annotation { "Feature Type Name" : "Feature", "Feature Type Description" : "" }
export const myFeature = defineFeature(function(context is Context, id is Id, definition is map)
    precondition{}
    {
        {
            var Q0;
            Q0=qCreatedBy(makeId("Top.planeOp"),FACE);
            var sketch = newSketch(context, id + "F0", { "sketchPlane" : qUnion([Q0])});
            skLineSegment(sketch, "E0.bottom", {"start": v(-44.45, 25.4) * mm, "end": v(44.45, 25.4) * mm});
            skLineSegment(sketch, "E0.top", {"start": v(-44.45, -25.4) * mm, "end": v(44.45, -25.4) * mm});
            skLineSegment(sketch, "E0.left", {"start": v(-44.45, 25.4) * mm, "end": v(-44.45, -25.4) * mm});
            skLineSegment(sketch, "E0.right", {"start": v(44.45, 25.4) * mm, "end": v(44.45, -25.4) * mm});
            skPoint(sketch, "E0.middle", {"position": v(0, 0) * mm});
            skSolve(sketch);
        }
        {
            var Q0;
            Q0=makeQuery(id+"F0.imprint","IMPRINT",FACE,{"disambiguationData":[TD([[makeQuery(id+"F0.imprint","IMPRINT",EDGE,{"derivedFrom":sQuery(id+"F0.wireOp",EDGE,"E0.bottom")}),-1.0]])]});
            extrude(context, id + "F1", {"entities" : qUnion([Q0]), "depth" : 1 * mm, "offsetDistance" : 25 * mm});
        }
        {
            var Q0;
            Q0=makeQuery(id+"F1.opExtrude","CAP_FACE",FACE,{"disambiguationData":[OSD([sQuery(id+"F0.wireOp",EDGE,"E0.bottom"),sQuery(id+"F0.wireOp",EDGE,"E0.top"),sQuery(id+"F0.wireOp",EDGE,"E0.left"),sQuery(id+"F0.wireOp",EDGE,"E0.right")])],"isStart":false});
            var sketch = newSketch(context, id + "F2", { "sketchPlane" : qUnion([Q0])});
            skText(sketch, "E1", { "text": "Andrea Szikszay", "fontName": "AllertaStencil-Regular.ttf"});
            skText(sketch, "E2", { "text": "Engineering Student", "fontName": "AllertaStencil-Regular.ttf"});
            skText(sketch, "E3", { "text": "C: 813 368 4735\<email>", "fontName": "AllertaStencil-Regular.ttf"});
            const initialGuessF2  = {"E1": [-0.03975, 0.0119, 1, 0, 0.00609], "E2": [-0.03975, 0.0037, 1, 0, 0.00422], "E3": [-0.03975, -0.01407, 1, 0, 0.00352]};
            skSetInitialGuess(sketch, initialGuessF2);
            skSolve(sketch);
        }
        {
            var Q0;
            Q0 = qSketchRegion(id + "F2", true);
            extrude(context, id + "F3", {"entities" : qUnion([Q0]), "operationType" : NewBodyOperationType.REMOVE, "endBound" : BoundingType.THROUGH_ALL, "oppositeDirection" : true, "depth" : 0.5 * mm, "offsetDistance" : 25 * mm});
        }
        {
            var Q0;
            {var subQ0=sQuery(id+"F0.wireOp",EDGE,"E0.bottom");var subQ1=sQuery(id+"F0.wireOp",EDGE,"E0.top");var subQ2=sQuery(id+"F0.wireOp",EDGE,"E0.left");var subQ3=sQuery(id+"F0.wireOp",EDGE,"E0.right");Q0=makeQuery(id+"F3.boolean.opBoolean","SPLIT",FACE,{"disambiguationData":[TD([makeQuery(id+"F1.opExtrude","SWEPT_FACE",FACE,{"disambiguationData":[OSD([subQ0])]})])],"derivedFrom":makeQuery(id+"F1.opExtrude","CAP_FACE",FACE,{"disambiguationData":[OSD([subQ0,subQ1,subQ2,subQ3])],"isStart":false})});}
            var sketch = newSketch(context, id + "F4", { "sketchPlane" : qUnion([Q0])});
            skCircle(sketch, "E4", {"center": v(40.29, 20.44) * mm, "radius": 1.75 * mm});
            skFitSpline(sketch, "E5", {"points": [v(42.4, 20.71) * mm, v(43.2, 21.1) * mm, v(43.65, 20.91) * mm, v(43.3, 20.56) * mm, v(42.4, 20.71) * mm]});
            skFitSpline(sketch, "E6", {"points": [v(42.47, 19.63) * mm, v(43.35, 19.68) * mm, v(43.65, 19.2) * mm, v(43.23, 19.15) * mm, v(42.47, 19.63) * mm]});
            skFitSpline(sketch, "E7", {"points": [v(41.94, 18.85) * mm, v(42.72, 18.54) * mm, v(42.72, 18.14) * mm, v(42.22, 18.19) * mm, v(41.94, 18.85) * mm]});
            skFitSpline(sketch, "E8", {"points": [v(41.06, 18.44) * mm, v(41.56, 17.91) * mm, v(41.38, 17.18) * mm, v(40.9, 17.48) * mm, v(41.06, 18.44) * mm]});
            skFitSpline(sketch, "E9", {"points": [v(39.97, 18.27) * mm, v(40.2, 17.6) * mm, v(39.87, 17.18) * mm, v(39.54, 17.58) * mm, v(39.97, 18.27) * mm]});
            skFitSpline(sketch, "E10", {"points": [v(38.96, 18.74) * mm, v(38.7, 17.94) * mm, v(38.15, 17.94) * mm, v(38.2, 18.42) * mm, v(38.96, 18.74) * mm]});
            skFitSpline(sketch, "E11", {"points": [v(38.36, 19.65) * mm, v(38, 19.2) * mm, v(37.47, 19.12) * mm, v(37.47, 19.43) * mm, v(38.36, 19.65) * mm]});
            skFitSpline(sketch, "E12", {"points": [v(38.13, 20.54) * mm, v(37.45, 20.3) * mm, v(36.94, 20.56) * mm, v(37.3, 20.84) * mm, v(38.13, 20.54) * mm]});
            skFitSpline(sketch, "E13", {"points": [v(38.5, 21.7) * mm, v(37.75, 21.72) * mm, v(37.52, 22.15) * mm, v(37.95, 22.23) * mm, v(38.5, 21.7) * mm]});
            skFitSpline(sketch, "E14", {"points": [v(39.16, 22.3) * mm, v(38.53, 22.5) * mm, v(38.5, 22.98) * mm, v(38.89, 22.96) * mm, v(39.16, 22.3) * mm]});
            skFitSpline(sketch, "E15", {"points": [v(39.95, 22.55) * mm, v(39.57, 23.08) * mm, v(39.7, 23.69) * mm, v(40.15, 23.41) * mm, v(39.95, 22.55) * mm]});
            skFitSpline(sketch, "E16", {"points": [v(40.9, 22.5) * mm, v(40.84, 23.38) * mm, v(41.3, 23.7) * mm, v(41.54, 23.27) * mm, v(40.9, 22.5) * mm]});
            skFitSpline(sketch, "E17", {"points": [v(41.99, 21.84) * mm, v(42.37, 22.65) * mm, v(43.06, 22.67) * mm, v(43.04, 22.23) * mm, v(41.99, 21.84) * mm]});
            skFitSpline(sketch, "E18", {"points": [v(42.44, 17.04) * mm, v(43.25, 10.05) * mm, v(40.73, -24.15) * mm, v(39.76, -23.74) * mm, v(40.49, -23.01) * mm, v(42.85, 3.64) * mm, v(41.98, 16.43) * mm, v(42.44, 17.04) * mm]});
            skFitSpline(sketch, "E19", {"points": [v(42.64, 6.87) * mm, v(40.68, 8.3) * mm, v(40.1, 7.98) * mm, v(41.12, 7.2) * mm, v(42.64, 6.87) * mm]});
            skSolve(sketch);
        }
        {
            var Q0;
            Q0 = qSketchRegion(id + "F4", true);
            extrude(context, id + "F5", {"entities" : qUnion([Q0]), "operationType" : NewBodyOperationType.REMOVE, "oppositeDirection" : true, "depth" : 25 * mm, "offsetDistance" : 25 * mm});
        }
        {
            var Q0;
            {var subQ0=sQuery(id+"F0.wireOp",EDGE,"E0.bottom");var subQ1=sQuery(id+"F0.wireOp",EDGE,"E0.top");var subQ2=sQuery(id+"F0.wireOp",EDGE,"E0.left");var subQ3=sQuery(id+"F0.wireOp",EDGE,"E0.right");Q0=makeQuery(id+"F3.boolean.opBoolean","SPLIT",FACE,{"disambiguationData":[TD([makeQuery(id+"F1.opExtrude","SWEPT_FACE",FACE,{"disambiguationData":[OSD([subQ0])]})])],"derivedFrom":makeQuery(id+"F1.opExtrude","CAP_FACE",FACE,{"disambiguationData":[OSD([subQ0,subQ1,subQ2,subQ3])],"isStart":false})});}
            var sketch = newSketch(context, id + "F6", { "sketchPlane" : qUnion([Q0])});
            skCircle(sketch, "E20", {"center": v(38.48, 14.45) * mm, "radius": 1.5 * mm});
            skFitSpline(sketch, "E21", {"points": [v(40.28, 14.68) * mm, v(40.98, 15) * mm, v(41.37, 14.85) * mm, v(41.06, 14.55) * mm, v(40.28, 14.68) * mm]});
            skFitSpline(sketch, "E22", {"points": [v(40.35, 13.75) * mm, v(41.1, 13.8) * mm, v(41.37, 13.38) * mm, v(41, 13.34) * mm, v(40.35, 13.75) * mm]});
            skFitSpline(sketch, "E23", {"points": [v(39.9, 13.08) * mm, v(40.57, 12.82) * mm, v(40.57, 12.47) * mm, v(40.13, 12.52) * mm, v(39.9, 13.08) * mm]});
            skFitSpline(sketch, "E24", {"points": [v(39.14, 12.73) * mm, v(39.57, 12.28) * mm, v(39.42, 11.65) * mm, v(39, 11.91) * mm, v(39.14, 12.73) * mm]});
            skFitSpline(sketch, "E25", {"points": [v(38.2, 12.58) * mm, v(38.4, 12.02) * mm, v(38.12, 11.65) * mm, v(37.84, 12) * mm, v(38.2, 12.58) * mm]});
            skFitSpline(sketch, "E26", {"points": [v(37.34, 13) * mm, v(37.13, 12.3) * mm, v(36.65, 12.3) * mm, v(36.7, 12.71) * mm, v(37.34, 13) * mm]});
            skFitSpline(sketch, "E27", {"points": [v(36.82, 13.77) * mm, v(36.52, 13.38) * mm, v(36.07, 13.32) * mm, v(36.07, 13.58) * mm, v(36.82, 13.77) * mm]});
            skFitSpline(sketch, "E28", {"points": [v(36.63, 14.53) * mm, v(36.05, 14.33) * mm, v(35.61, 14.55) * mm, v(35.92, 14.79) * mm, v(36.63, 14.53) * mm]});
            skFitSpline(sketch, "E29", {"points": [v(36.95, 15.52) * mm, v(36.3, 15.55) * mm, v(36.11, 15.91) * mm, v(36.48, 15.98) * mm, v(36.95, 15.52) * mm]});
            skFitSpline(sketch, "E30", {"points": [v(37.52, 16.04) * mm, v(36.98, 16.22) * mm, v(36.95, 16.63) * mm, v(37.28, 16.6) * mm, v(37.52, 16.04) * mm]});
            skFitSpline(sketch, "E31", {"points": [v(38.19, 16.26) * mm, v(37.86, 16.71) * mm, v(37.97, 17.23) * mm, v(38.36, 17) * mm, v(38.19, 16.26) * mm]});
            skFitSpline(sketch, "E32", {"points": [v(39, 16.2) * mm, v(38.95, 16.97) * mm, v(39.35, 17.24) * mm, v(39.55, 16.87) * mm, v(39, 16.2) * mm]});
            skFitSpline(sketch, "E33", {"points": [v(39.94, 15.65) * mm, v(40.26, 16.34) * mm, v(40.85, 16.35) * mm, v(40.84, 15.98) * mm, v(39.94, 15.65) * mm]});
            skFitSpline(sketch, "E34", {"points": [v(39.2, 10.97) * mm, v(35.1, -7.56) * mm, v(34.84, -23.3) * mm, v(36.05, -23.2) * mm, v(35.04, -21.42) * mm, v(38.45, 7.4) * mm, v(39.39, 10.9) * mm, v(39.2, 10.97) * mm]});
            skFitSpline(sketch, "E35", {"points": [v(37.25, 2.33) * mm, v(38.56, 2.97) * mm, v(39.29, 2.56) * mm, v(38.68, 2.36) * mm, v(37.25, 2.33) * mm]});
            skSolve(sketch);
        }
        {
            var Q0;
            Q0 = qSketchRegion(id + "F6", true);
            extrude(context, id + "F7", {"entities" : qUnion([Q0]), "operationType" : NewBodyOperationType.REMOVE, "oppositeDirection" : true, "depth" : 25 * mm, "offsetDistance" : 25 * mm});
        }
        {
            var Q0;
            {var subQ0=sQuery(id+"F0.wireOp",EDGE,"E0.bottom");var subQ1=sQuery(id+"F0.wireOp",EDGE,"E0.top");var subQ2=sQuery(id+"F0.wireOp",EDGE,"E0.left");var subQ3=sQuery(id+"F0.wireOp",EDGE,"E0.right");Q0=makeQuery(id+"F3.boolean.opBoolean","SPLIT",FACE,{"disambiguationData":[TD([makeQuery(id+"F1.opExtrude","SWEPT_FACE",FACE,{"disambiguationData":[OSD([subQ0])]})])],"derivedFrom":makeQuery(id+"F1.opExtrude","CAP_FACE",FACE,{"disambiguationData":[OSD([subQ0,subQ1,subQ2,subQ3])],"isStart":false})});}
            var sketch = newSketch(context, id + "F8", { "sketchPlane" : qUnion([Q0])});
            skCircle(sketch, "E36", {"center": v(34.22, 19.43) * mm, "radius": 1.25 * mm});
            skFitSpline(sketch, "E37", {"points": [v(35.72, 19.63) * mm, v(36.3, 19.9) * mm, v(36.62, 19.77) * mm, v(36.37, 19.52) * mm, v(35.72, 19.63) * mm]});
            skFitSpline(sketch, "E38", {"points": [v(35.78, 18.85) * mm, v(36.4, 18.89) * mm, v(36.62, 18.55) * mm, v(36.32, 18.5) * mm, v(35.78, 18.85) * mm]});
            skFitSpline(sketch, "E39", {"points": [v(35.4, 18.3) * mm, v(35.96, 18.08) * mm, v(35.96, 17.79) * mm, v(35.6, 17.83) * mm, v(35.4, 18.3) * mm]});
            skFitSpline(sketch, "E40", {"points": [v(34.77, 18) * mm, v(35.13, 17.63) * mm, v(35, 17.1) * mm, v(34.66, 17.32) * mm, v(34.77, 18) * mm]});
            skFitSpline(sketch, "E41", {"points": [v(34, 17.88) * mm, v(34.16, 17.41) * mm, v(33.92, 17.1) * mm, v(33.69, 17.4) * mm, v(34, 17.88) * mm]});
            skFitSpline(sketch, "E42", {"points": [v(33.27, 18.22) * mm, v(33.1, 17.64) * mm, v(32.7, 17.64) * mm, v(32.73, 17.99) * mm, v(33.27, 18.22) * mm]});
            skFitSpline(sketch, "E43", {"points": [v(32.84, 18.87) * mm, v(32.59, 18.55) * mm, v(32.2, 18.5) * mm, v(32.2, 18.7) * mm, v(32.84, 18.87) * mm]});
            skFitSpline(sketch, "E44", {"points": [v(32.68, 19.5) * mm, v(32.2, 19.34) * mm, v(31.83, 19.52) * mm, v(32.08, 19.72) * mm, v(32.68, 19.5) * mm]});
            skFitSpline(sketch, "E45", {"points": [v(32.95, 20.33) * mm, v(32.4, 20.35) * mm, v(32.25, 20.65) * mm, v(32.55, 20.7) * mm, v(32.95, 20.33) * mm]});
            skFitSpline(sketch, "E46", {"points": [v(33.42, 20.76) * mm, v(32.97, 20.9) * mm, v(32.95, 21.25) * mm, v(33.22, 21.23) * mm, v(33.42, 20.76) * mm]});
            skFitSpline(sketch, "E47", {"points": [v(33.97, 20.94) * mm, v(33.7, 21.32) * mm, v(33.8, 21.75) * mm, v(34.12, 21.56) * mm, v(33.97, 20.94) * mm]});
            skFitSpline(sketch, "E48", {"points": [v(34.65, 20.9) * mm, v(34.61, 21.53) * mm, v(34.95, 21.76) * mm, v(35.11, 21.45) * mm, v(34.65, 20.9) * mm]});
            skFitSpline(sketch, "E49", {"points": [v(35.43, 20.43) * mm, v(35.7, 21) * mm, v(36.2, 21.02) * mm, v(36.18, 20.71) * mm, v(35.43, 20.43) * mm]});
            skFitSpline(sketch, "E50", {"points": [v(34.07, 12.76) * mm, v(33.84, 8.42) * mm, v(36.6, 2.93) * mm, v(36.66, 3.02) * mm, v(34.86, 6.28) * mm, v(33.9, 9.43) * mm, v(34.07, 12.76) * mm]});
            skFitSpline(sketch, "E51", {"points": [v(34.64, 16.73) * mm, v(34.97, 16.76) * mm, v(34.16, 13.1) * mm, v(34.62, 15.33) * mm, v(34.64, 16.73) * mm]});
            skFitSpline(sketch, "E52", {"points": [v(38.07, 1.99) * mm, v(40.62, -1.73) * mm, v(38.46, -23.61) * mm, v(37.9, -23.47) * mm, v(39.44, -17.17) * mm, v(40.42, -3.67) * mm, v(38.07, 1.99) * mm]});
            skFitSpline(sketch, "E53", {"points": [v(40.18, -2.9) * mm, v(39.07, -2.3) * mm, v(38.42, -2.53) * mm, v(39.07, -2.83) * mm, v(40.18, -2.9) * mm]});
            skFitSpline(sketch, "E54", {"points": [v(33.91, 10.14) * mm, v(34.82, 10.83) * mm, v(35.4, 10.87) * mm, v(35.1, 10.48) * mm, v(33.91, 10.14) * mm]});
            skSolve(sketch);
        }
        {
            var Q0;
            Q0 = qSketchRegion(id + "F8", true);
            extrude(context, id + "F9", {"entities" : qUnion([Q0]), "operationType" : NewBodyOperationType.REMOVE, "oppositeDirection" : true, "depth" : 25 * mm, "offsetDistance" : 25 * mm});
        }
    });